# Revit family: Overhead_Door-CHI_Overhead_Doors-Counter_Shutter-7500
name_source: partatom
category: Specialty Equipment
units: mm (PartAtom-declared; Revit-internal decimal feet)

## family parameters
Always vertical = Yes
Classification Number = 23.30.10.21
Cut with Voids When Loaded = No
Enable Cutting in Views = No
Host = Wall
Maintain Annotation Orientation = No
Part Type = Normal
Room Calculation Point = No
Round Connector Dimension = Use Diameter
Shared = No

## types (4) — shared parameters
Apparent Load Phase 1 = 0 VA
Apparent Load Phase 2 = 0 VA
Apparent Load Phase 3 = 0 VA
Assembly Code = B2030410
Back Room = 0' - 11 1/2"
Default Elevation = 2' - 4"
Description = Fire Shutter Door
Fire Rating = 3/4 Hr | 1-1/2 Hr | 3 Hr
Keynote = 08 30 00
Load Classification = Motor
Manufacturer = C.H.I. Overhead Doors
Manufacturer Fax Number = 800-677-2650
Number of Poles = 1
Panel Thickness = 0' - 0 1/2"
Product Documentation Link = https://cdn2.hubspot.net
Product Page URL = https://www.chiohd.com
Shutter Box Bottom Gap = 0' - 1 1/2"
Steel Gauge = min. 22
URL = https://www.chiohd.com
Version = 2021-v1.a
Voltage = 0 V
Warranty URL = https://www.chiohd.com

## per-type parameters (varying)
| type | C Model | Guides Material | Locks Material | Material | Model | Panel Finish |
| Fire Counter Shutter - 7522 - Gray - F1.5 Flat Slat | 1 | Steel - C.H.I Overhead Doors - Unpainted Galvanized | Steel - C.H.I Overhead Door - Plated | Steel - C.H.I Overhead Doors - Unpainted Galvanized | 7522 | Steel - C.H.I Overhead Doors - F1.5 Flat Slat - Unpainted Galvanized |
| Fire Counter Shutter - 7566 - Stainless Steel - F1.5 Flat Slat | 2 | Steel - C.H.I Overhead Doors - Stainless | Steel - C.H.I Overhead Doors - Stainless | Steel - C.H.I Overhead Doors - Stainless | 7566 | Steel - C.H.I Overhead Doors - F1.5 Flat Slat - Stainless |
| Fire Counter Shutter - 7522 - White - F1.5 Flat Slat | 1 | Steel - C.H.I Overhead Doors - White | Steel - C.H.I Overhead Door - Plated | Steel - C.H.I Overhead Doors - White | 7522 | Steel - C.H.I Overhead Doors - F1.5 Flat Slat - White |
| Fire Counter Shutter - 7522 - Galvanized - F1.5 Flat Slat | 1 | Steel - C.H.I Overhead Doors - Unpainted Galvanized | Steel - C.H.I Overhead Door - Plated | Steel - C.H.I Overhead Doors - Unpainted Galvanized | 7522 | Steel - C.H.I Overhead Doors - F1.5 Flat Slat - Unpainted Galvanized |

## geometry (parser evidence)
native form markers: Sweep x10
no freeform markers — native parametric forms only
